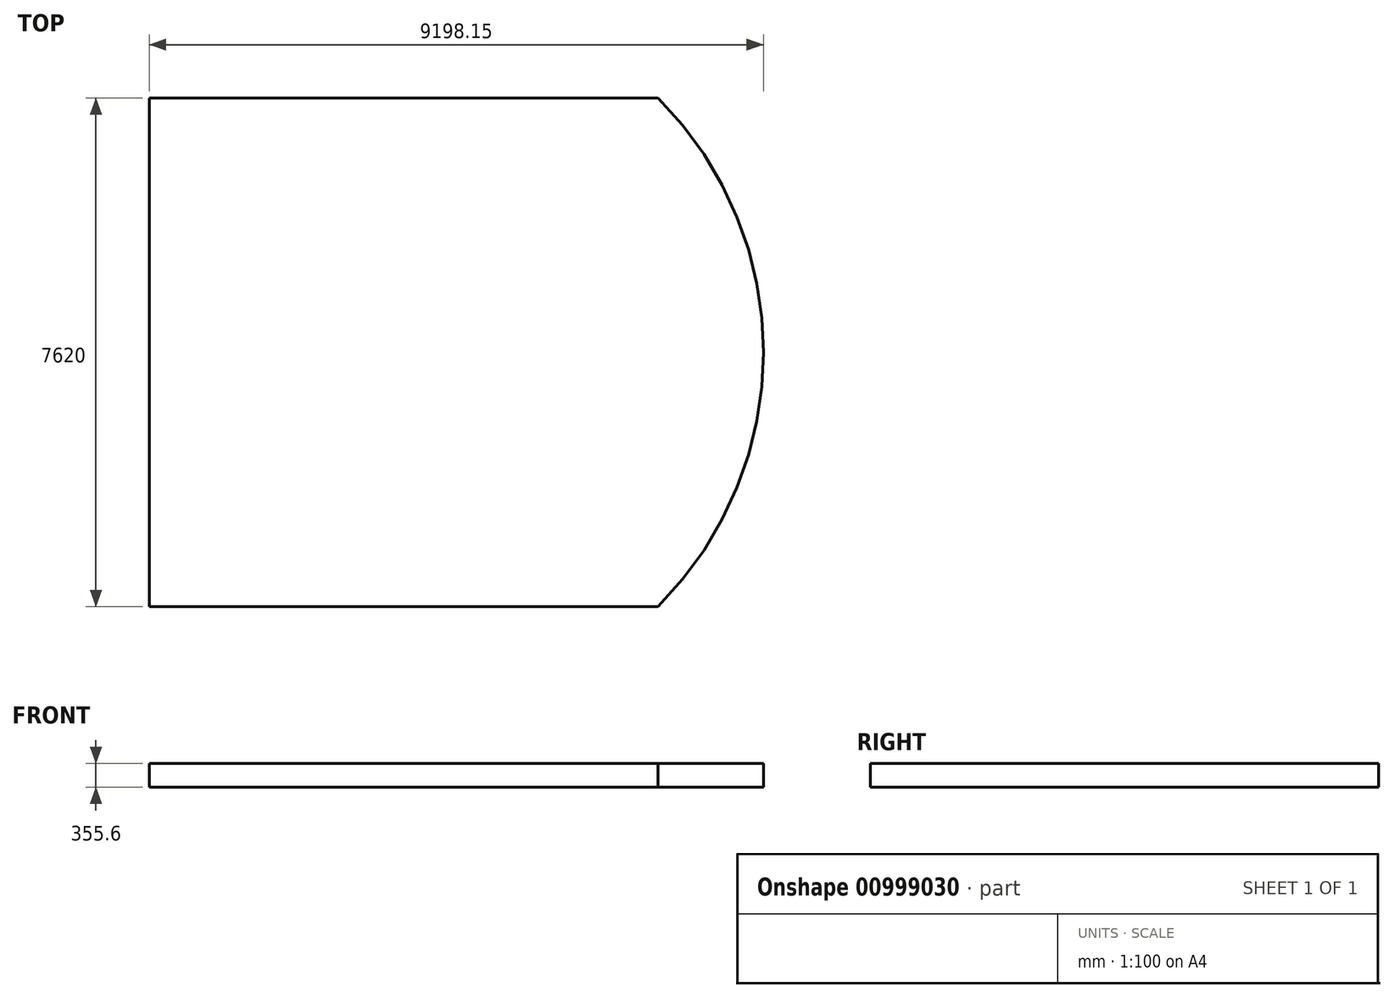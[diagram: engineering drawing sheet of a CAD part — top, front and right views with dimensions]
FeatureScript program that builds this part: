
annotation { "Feature Type Name" : "Feature", "Feature Type Description" : "" }
export const myFeature = defineFeature(function(context is Context, id is Id, definition is map)
    precondition{}
    {
        {
            var Q0;
            Q0=qCreatedBy(makeId("Top.planeOp"),FACE);
            var sketch = newSketch(context, id + "F0", { "sketchPlane" : qUnion([Q0])});
            skLineSegment(sketch, "E0.bottom", {"start": v(-3810, 3810) * mm, "end": v(3810, 3810) * mm});
            skLineSegment(sketch, "E0.top", {"start": v(-3810, -3810) * mm, "end": v(3810, -3810) * mm});
            skLineSegment(sketch, "E0.left", {"start": v(-3810, 3810) * mm, "end": v(-3810, -3810) * mm});
            skLineSegment(sketch, "E0.right", {"start": v(3810, 3810) * mm, "end": v(3810, -3810) * mm});
            skPoint(sketch, "E0.middle", {"position": v(0, 0) * mm});
            skArc(sketch, "E1", {"start": v(3810, 3810) * mm, "mid": v(5388.15, 0) * mm, "end": v(3810, -3810) * mm});
            skSolve(sketch);
        }
        {
            var Q0;
            Q0=makeQuery(id+"F0.imprint","IMPRINT",FACE,{"disambiguationData":[TD([[makeQuery(id+"F0.imprint","IMPRINT",EDGE,{"derivedFrom":sQuery(id+"F0.wireOp",EDGE,"E0.bottom")}),-1.0]])]});
            var Q1;
            Q1=makeQuery(id+"F0.imprint","IMPRINT",FACE,{"disambiguationData":[TD([[makeQuery(id+"F0.imprint","IMPRINT",EDGE,{"derivedFrom":sQuery(id+"F0.wireOp",EDGE,"E0.right")}),1.0]])]});
            extrude(context, id + "F1", {"entities" : qUnion([Q0, Q1]), "depth" : 355.6 * mm, "offsetDistance" : 25.4 * mm});
        }
    });
